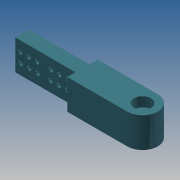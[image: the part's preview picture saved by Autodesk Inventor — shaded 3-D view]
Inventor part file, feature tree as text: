
AUTODESK INVENTOR PART (.ipt)
format: ipt  version: 2013 (Build 170138000, 138)  size: 172,544 bytes
history: native  units: mm
features: extrude x8, sketch x8, fillet x1
ambient origin geometry x8: Origin, YZ Plane, XZ Plane, XY Plane, X Axis, Y Axis, Z Axis, Center Point
bodies: Solid1 (feature_tree)
feature tree (17):
  extrude  "Extrusion1"  Depth=12.6mm
  extrude  "Extrusion2"  Depth=8.5mm
  extrude  "Extrusion3"  Depth=22.0mm
  extrude  "Extrusion4"  Depth=20.0mm
  extrude  "Extrusion5"  Depth=7.0mm TaperAngle=0.0deg
  extrude  "Extrusion6"  Depth=3.5mm
  fillet  "Fillet1"  Radius=35.0mm
  extrude  "Extrusion7"  Depth=6.0mm
  extrude  "Extrusion8"  Depth=8.0mm TaperAngle=0.0deg
  sketch  "Sketch1"  dims[d0=153.0mm d2=12.6mm]
  sketch  "Sketch2"  dims[d3=15.0mm d4=8.5mm]
  sketch  "Sketch4"  dims[d5=25.0mm d6=0.0mm d7=22.0mm]
  sketch  "Sketch5"  dims[d9=7.0mm d10=0.0mm d16=20.0mm]
  sketch  "Sketch6"  dims[d17=40.0mm d18=7.0mm d19=0.0mm]
  sketch  "Sketch7"  dims[d21=3.0mm d22=0.0mm d23=3.5mm d24=35.0mm]
  sketch  "Sketch8"  dims[d26=10.0mm d27=0.0mm d28=6.0mm]
  sketch  "Sketch9"  dims[d30=14.0mm d32=8.0mm d33=0.0mm d34=3.5mm d35=50.0mm d36=50.0mm d37=11.5mm d38=10.0mm d39=0.0mm d40=12.5mm d41=8.0mm d42=0.5mm d43=1.0mm d44=1.5mm d45=2.0mm d46=2.5mm d47=3.5mm d48=25.0mm d49=0.5mm d50=1.0mm d51=1.5mm d52=2.0mm d53=2.5mm d54=10.0mm d55=0.0mm]
